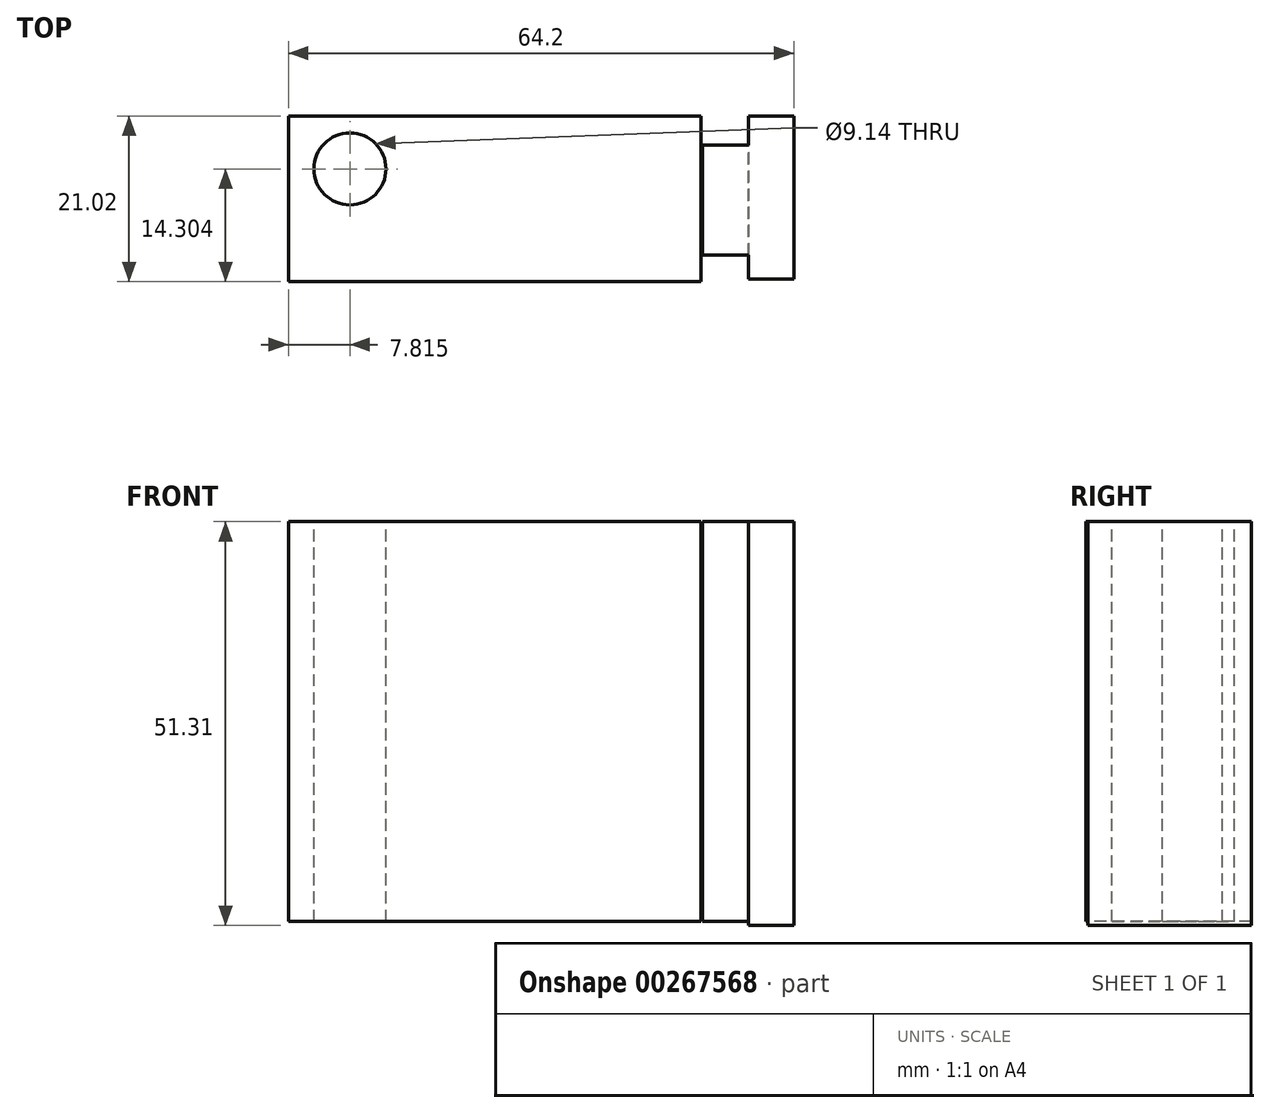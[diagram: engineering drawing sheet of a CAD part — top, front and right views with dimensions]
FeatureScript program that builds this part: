
annotation { "Feature Type Name" : "Feature", "Feature Type Description" : "" }
export const myFeature = defineFeature(function(context is Context, id is Id, definition is map)
    precondition{}
    {
        {
            var Q0;
            Q0=qCreatedBy(makeId("Top.planeOp"),FACE);
            var sketch = newSketch(context, id + "F0", { "sketchPlane" : qUnion([Q0])});
            skLineSegment(sketch, "E0.bottom", {"start": v(-43.2, 0) * mm, "end": v(-14.05, 0) * mm});
            skLineSegment(sketch, "E0.top", {"start": v(-43.2, -37.58) * mm, "end": v(-14.05, -37.58) * mm});
            skLineSegment(sketch, "E0.left", {"start": v(-43.2, 0) * mm, "end": v(-43.2, -37.58) * mm});
            skLineSegment(sketch, "E0.right", {"start": v(-14.05, 0) * mm, "end": v(-14.05, -37.58) * mm});
            skSolve(sketch);
        }
        {
            var Q0;
            Q0 = qSketchRegion(id + "F0", true);
            var Q1;
            Q1=makeQuery(id+"F0.imprint","IMPRINT",FACE,{"disambiguationData":[TD([[makeQuery(id+"F0.imprint","IMPRINT",EDGE,{"derivedFrom":sQuery(id+"F0.wireOp",EDGE,"E0.bottom")}),-1.0]])]});
            extrude(context, id + "F1", {"entities" : qUnion([Q0, Q1]), "depth" : 25.4 * mm});
        }
        {
            var Q0;
            Q0=makeQuery(id+"F1.opExtrude","SWEPT_BODY",BODY,{"disambiguationData":[OSD([sQuery(id+"F0.wireOp",EDGE,"E0.bottom"),sQuery(id+"F0.wireOp",EDGE,"E0.top"),sQuery(id+"F0.wireOp",EDGE,"E0.left"),sQuery(id+"F0.wireOp",EDGE,"E0.right")])]});
            deleteBodies(context, id + "F2", {"entities" : qUnion([Q0])});
        }
        {
            var Q0;
            Q0=qCreatedBy(makeId("Top.planeOp"),FACE);
            var sketch = newSketch(context, id + "F3", { "sketchPlane" : qUnion([Q0])});
            skLineSegment(sketch, "E1.bottom", {"start": v(-46.22, 35.52) * mm, "end": v(6.18, 35.52) * mm});
            skLineSegment(sketch, "E1.top", {"start": v(-46.22, 14.5) * mm, "end": v(6.18, 14.5) * mm});
            skLineSegment(sketch, "E1.left", {"start": v(-46.22, 35.52) * mm, "end": v(-46.22, 14.5) * mm});
            skLineSegment(sketch, "E1.right", {"start": v(6.18, 35.52) * mm, "end": v(6.18, 14.5) * mm});
            skSolve(sketch);
        }
        {
            var Q0;
            Q0=makeQuery(id+"F3.imprint","IMPRINT",FACE,{"disambiguationData":[TD([[makeQuery(id+"F3.imprint","IMPRINT",EDGE,{"derivedFrom":sQuery(id+"F3.wireOp",EDGE,"E1.bottom")}),-1.0]])]});
            extrude(context, id + "F4", {"entities" : qUnion([Q0]), "oppositeDirection" : true, "depth" : 50.8 * mm});
        }
        {
            var Q0;
            Q0=makeQuery(id+"F4.opExtrude","CAP_FACE",FACE,{"disambiguationData":[OSD([sQuery(id+"F3.wireOp",EDGE,"E1.bottom"),sQuery(id+"F3.wireOp",EDGE,"E1.top"),sQuery(id+"F3.wireOp",EDGE,"E1.left"),sQuery(id+"F3.wireOp",EDGE,"E1.right")])],"isStart":true});
            var sketch = newSketch(context, id + "F5", { "sketchPlane" : qUnion([Q0])});
            skCircle(sketch, "E2", {"center": v(-38.4, 28.8) * mm, "radius": 4.57 * mm});
            skSolve(sketch);
        }
        {
            var Q0;
            Q0 = qSketchRegion(id + "F5", true);
            extrude(context, id + "F6", {"entities" : qUnion([Q0]), "operationType" : NewBodyOperationType.REMOVE, "oppositeDirection" : true, "depth" : 75.44 * mm});
        }
        {
            var Q0;
            Q0=qCreatedBy(makeId("Top.planeOp"),FACE);
            var sketch = newSketch(context, id + "F7", { "sketchPlane" : qUnion([Q0])});
            skLineSegment(sketch, "E3.bottom", {"start": v(6.4, 31.85) * mm, "end": v(12.2, 31.85) * mm});
            skLineSegment(sketch, "E3.top", {"start": v(6.4, 17.83) * mm, "end": v(12.2, 17.83) * mm});
            skLineSegment(sketch, "E3.left", {"start": v(6.4, 31.85) * mm, "end": v(6.4, 17.83) * mm});
            skLineSegment(sketch, "E3.right", {"start": v(12.2, 31.85) * mm, "end": v(12.2, 17.83) * mm});
            skSolve(sketch);
        }
        {
            var Q0;
            Q0=qCreatedBy(makeId("Top.planeOp"),FACE);
            var sketch = newSketch(context, id + "F8", { "sketchPlane" : qUnion([Q0])});
            skLineSegment(sketch, "E4.bottom", {"start": v(12.2, 35.5) * mm, "end": v(17.98, 35.5) * mm});
            skLineSegment(sketch, "E4.top", {"start": v(12.2, 14.78) * mm, "end": v(17.98, 14.78) * mm});
            skLineSegment(sketch, "E4.left", {"start": v(12.2, 35.5) * mm, "end": v(12.2, 14.78) * mm});
            skLineSegment(sketch, "E4.right", {"start": v(17.98, 35.5) * mm, "end": v(17.98, 14.78) * mm});
            skSolve(sketch);
        }
        {
            var Q0;
            Q0=makeQuery(id+"F7.imprint","IMPRINT",FACE,{"disambiguationData":[TD([[makeQuery(id+"F7.imprint","IMPRINT",EDGE,{"derivedFrom":sQuery(id+"F7.wireOp",EDGE,"E3.bottom")}),-1.0]])]});
            var Q1;
            Q1=makeQuery(id+"F4.opExtrude","CAP_FACE",FACE,{"disambiguationData":[OSD([sQuery(id+"F3.wireOp",EDGE,"E1.bottom"),sQuery(id+"F3.wireOp",EDGE,"E1.top"),sQuery(id+"F3.wireOp",EDGE,"E1.left"),sQuery(id+"F3.wireOp",EDGE,"E1.right")])],"isStart":false});
            extrude(context, id + "F9", {"entities" : qUnion([Q0]), "endBound" : BoundingType.UP_TO_SURFACE, "oppositeDirection" : true, "endBoundEntityFace" : qUnion([Q1]), "depth" : 45.72 * mm});
        }
        {
            var Q0;
            Q0=makeQuery(id+"F8.imprint","IMPRINT",FACE,{"disambiguationData":[TD([[makeQuery(id+"F8.imprint","IMPRINT",EDGE,{"derivedFrom":sQuery(id+"F8.wireOp",EDGE,"E4.bottom")}),-1.0]])]});
            extrude(context, id + "F10", {"entities" : qUnion([Q0]), "operationType" : NewBodyOperationType.ADD, "oppositeDirection" : true, "depth" : 51.3 * mm});
        }
    });
